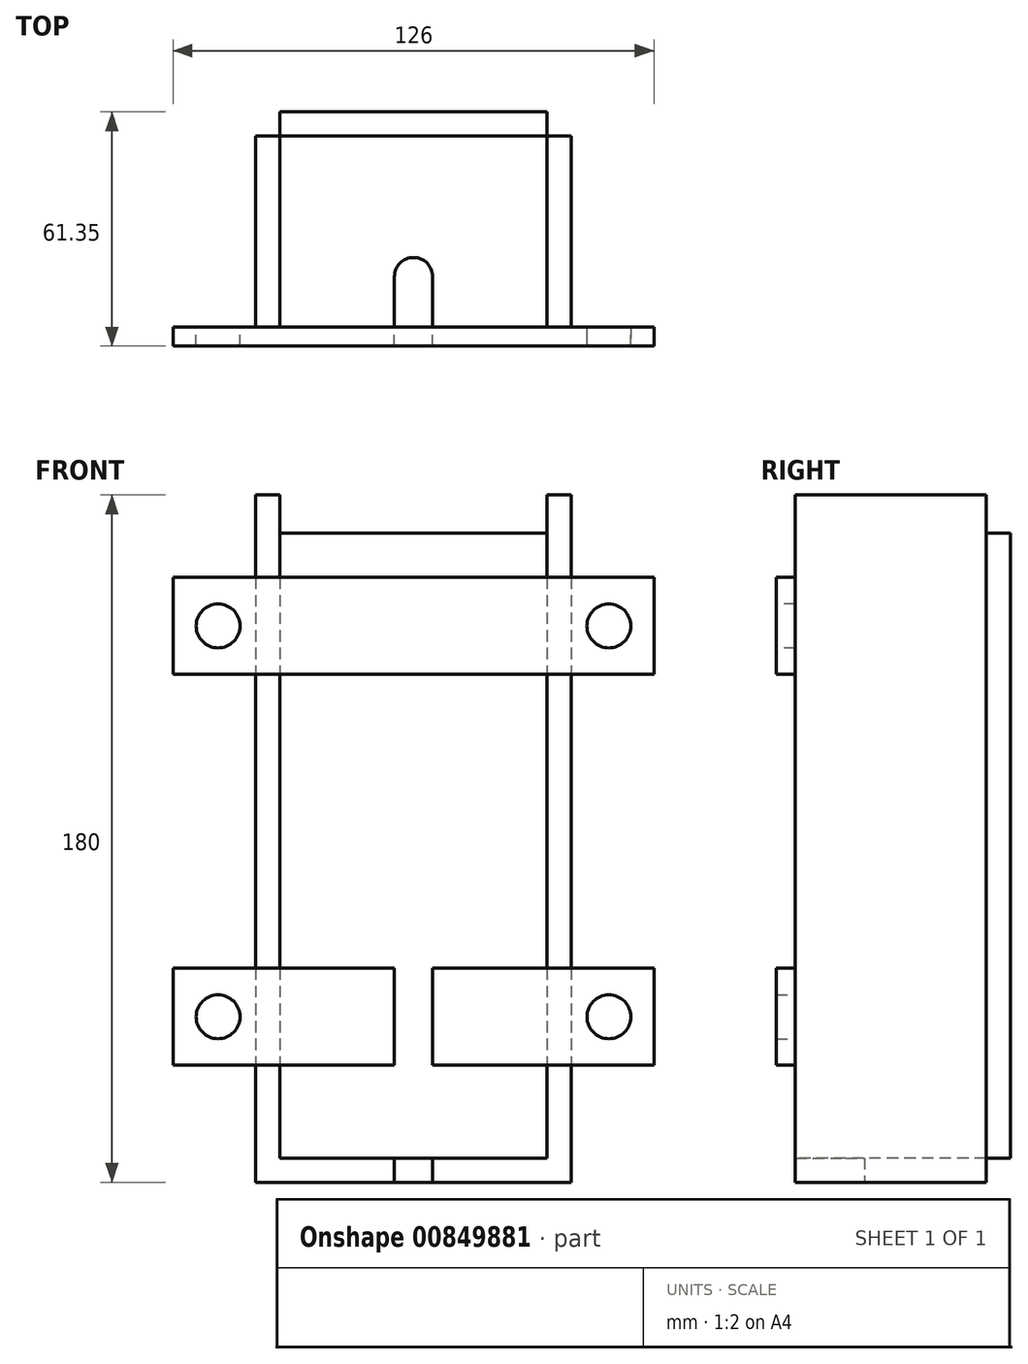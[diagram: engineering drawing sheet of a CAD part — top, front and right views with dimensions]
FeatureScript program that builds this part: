
annotation { "Feature Type Name" : "Feature", "Feature Type Description" : "" }
export const myFeature = defineFeature(function(context is Context, id is Id, definition is map)
    precondition{}
    {
        {
            var Q0;
            Q0=qCreatedBy(makeId("Top.planeOp"),FACE);
            var sketch = newSketch(context, id + "F0", { "sketchPlane" : qUnion([Q0])});
            skPoint(sketch, "E0.middle", {"position": v(0, 0) * mm});
            skLineSegment(sketch, "E1.bottom", {"start": v(35, 25) * mm, "end": v(-35, 25) * mm});
            skLineSegment(sketch, "E1.top", {"start": v(35, -25) * mm, "end": v(-35, -25) * mm});
            skLineSegment(sketch, "E1.left", {"start": v(35, 25) * mm, "end": v(35, -25) * mm});
            skLineSegment(sketch, "E1.right", {"start": v(-35, 25) * mm, "end": v(-35, -25) * mm});
            skLineSegment(sketch, "E2", {"start": v(0, -25) * mm, "end": v(-35, -25) * mm});
            skLineSegment(sketch, "E3", {"start": v(-35, -25) * mm, "end": v(-5, -25) * mm});
            skLineSegment(sketch, "E4", {"start": v(35, -25) * mm, "end": v(5, -25) * mm});
            skLineSegment(sketch, "E5", {"start": v(-5, -25) * mm, "end": v(-5, -11.8) * mm});
            skLineSegment(sketch, "E6", {"start": v(5, -25) * mm, "end": v(5, -11.8) * mm});
            skArc(sketch, "E7", {"start": v(-5, -11.8) * mm, "mid": v(0, -6.8) * mm, "end": v(5, -11.8) * mm});
            skSolve(sketch);
        }
        {
            var Q0;
            Q0=makeQuery(id+"F0.imprint","IMPRINT",FACE,{"disambiguationData":[TD([[makeQuery(id+"F0.imprint","IMPRINT",EDGE,{"derivedFrom":sQuery(id+"F0.wireOp",EDGE,"E1.bottom")}),1.0]])]});
            extrude(context, id + "F1", {"entities" : qUnion([Q0]), "depth" : 6.35 * mm, "offsetDistance" : 25 * mm});
        }
        {
            var Q0;
            Q0=makeQuery(id+"F1.opExtrude","SWEPT_FACE",FACE,{"disambiguationData":[OSD([sQuery(id+"F0.wireOp",EDGE,"E1.right")])]});
            var sketch = newSketch(context, id + "F2", { "sketchPlane" : qUnion([Q0])});
            skLineSegment(sketch, "E8.bottom", {"start": v(-25, 0) * mm, "end": v(25, 0) * mm});
            skLineSegment(sketch, "E8.top", {"start": v(-25, 180) * mm, "end": v(25, 180) * mm});
            skLineSegment(sketch, "E8.left", {"start": v(-25, 0) * mm, "end": v(-25, 180) * mm});
            skLineSegment(sketch, "E8.right", {"start": v(25, 0) * mm, "end": v(25, 180) * mm});
            skSolve(sketch);
        }
        {
            var Q0;
            Q0=qSketchRegion(id+"F2",true);
            extrude(context, id + "F3", {"entities" : qUnion([Q0]), "operationType" : NewBodyOperationType.ADD, "depth" : 6.35 * mm, "offsetDistance" : 25 * mm});
        }
        {
            var Q0;
            Q0=makeQuery(id+"F1.opExtrude","SWEPT_FACE",FACE,{"disambiguationData":[OSD([sQuery(id+"F0.wireOp",EDGE,"E1.left")])]});
            var sketch = newSketch(context, id + "F4", { "sketchPlane" : qUnion([Q0])});
            skLineSegment(sketch, "E9.bottom", {"start": v(-25, 0) * mm, "end": v(25, 0) * mm});
            skLineSegment(sketch, "E9.top", {"start": v(-25, 180) * mm, "end": v(25, 180) * mm});
            skLineSegment(sketch, "E9.left", {"start": v(-25, 0) * mm, "end": v(-25, 180) * mm});
            skLineSegment(sketch, "E9.right", {"start": v(25, 0) * mm, "end": v(25, 180) * mm});
            skSolve(sketch);
        }
        {
            var Q0;
            Q0=qSketchRegion(id+"F4",true);
            extrude(context, id + "F5", {"entities" : qUnion([Q0]), "operationType" : NewBodyOperationType.ADD, "depth" : 6.35 * mm, "offsetDistance" : 25 * mm});
        }
        {
            var Q0;
            Q0=makeQuery(id+"F5.boolean.opBoolean","MERGE",FACE,{"derivedFrom":[makeQuery(id+"F3.boolean.opBoolean","MERGE",FACE,{"derivedFrom":[makeQuery(id+"F1.opExtrude","SWEPT_FACE",FACE,{"disambiguationData":[OSD([sQuery(id+"F0.wireOp",EDGE,"E1.bottom")])]}),makeQuery(id+"F3.opExtrude","SWEPT_FACE",FACE,{"disambiguationData":[OSD([sQuery(id+"F2.wireOp",EDGE,"E8.left")])]})]}),makeQuery(id+"F5.opExtrude","SWEPT_FACE",FACE,{"disambiguationData":[OSD([sQuery(id+"F4.wireOp",EDGE,"E9.right")])]})]});
            var sketch = newSketch(context, id + "F6", { "sketchPlane" : qUnion([Q0])});
            skLineSegment(sketch, "E10.bottom", {"start": v(41.35, 0) * mm, "end": v(-41.35, 0) * mm});
            skLineSegment(sketch, "E10.top", {"start": v(41.35, 180) * mm, "end": v(-41.35, 180) * mm});
            skLineSegment(sketch, "E10.left", {"start": v(41.35, 0) * mm, "end": v(41.35, 180) * mm});
            skLineSegment(sketch, "E10.right", {"start": v(-41.35, 0) * mm, "end": v(-41.35, 180) * mm});
            skLineSegment(sketch, "E11.bottom", {"start": v(-41.35, 0) * mm, "end": v(41.35, 0) * mm});
            skLineSegment(sketch, "E11.top", {"start": v(-41.35, 170) * mm, "end": v(41.35, 170) * mm});
            skLineSegment(sketch, "E11.left", {"start": v(-41.35, 0) * mm, "end": v(-41.35, 170) * mm});
            skLineSegment(sketch, "E11.right", {"start": v(41.35, 0) * mm, "end": v(41.35, 170) * mm});
            skSolve(sketch);
        }
        {
            var Q0;
            {var subQ5=makeQuery(id+"F1.opExtrude","CAP_EDGE",EDGE,{"disambiguationData":[OSD([sQuery(id+"F0.wireOp",EDGE,"E1.bottom")])],"isStart":false});Q0=makeQuery(id+"F6.imprint","IMPRINT",FACE,{"disambiguationData":[TD([[makeQuery(id+"F6.imprint","IMPRINT",EDGE,{"derivedFrom":subQ5}),1.0]])]});}
            var Q1;
            Q1=makeQuery(id+"F6.imprint","IMPRINT",FACE,{"disambiguationData":[TD([[makeQuery(id+"F6.imprint","IMPRINT",EDGE,{"derivedFrom":sQuery(id+"F6.wireOp",EDGE,"E11.bottom")}),1.0]])]});
            var Q2;
            Q2=qSketchRegion(id+"F8",true);
            extrude(context, id + "F7", {"entities" : qUnion([Q0, Q1, Q2]), "operationType" : NewBodyOperationType.ADD, "depth" : 6.35 * mm, "offsetDistance" : 25 * mm});
        }
        {
            var Q0;
            Q0=makeQuery(id+"F5.boolean.opBoolean","MERGE",FACE,{"derivedFrom":[makeQuery(id+"F1.opExtrude","SWEPT_FACE",FACE,{"disambiguationData":[OSD([sQuery(id+"F0.wireOp",EDGE,"E4")])]}),makeQuery(id+"F5.opExtrude","SWEPT_FACE",FACE,{"disambiguationData":[OSD([sQuery(id+"F4.wireOp",EDGE,"E9.left")])]})]});
            var sketch = newSketch(context, id + "F8", { "sketchPlane" : qUnion([Q0])});
            skLineSegment(sketch, "E12", {"start": v(5, 6.35) * mm, "end": v(5, 43.33) * mm});
            skLineSegment(sketch, "E13", {"start": v(5, 43.33) * mm, "end": v(51.2, 43.33) * mm});
            skLineSegment(sketch, "E14", {"start": v(5, 6.35) * mm, "end": v(5, 30.62) * mm});
            skLineSegment(sketch, "E15.bottom", {"start": v(5, 30.62) * mm, "end": v(63, 30.62) * mm});
            skLineSegment(sketch, "E15.top", {"start": v(5, 56.03) * mm, "end": v(63, 56.03) * mm});
            skLineSegment(sketch, "E15.left", {"start": v(5, 30.62) * mm, "end": v(5, 56.03) * mm});
            skLineSegment(sketch, "E15.right", {"start": v(63, 30.63) * mm, "end": v(63, 56.02) * mm});
            skCircle(sketch, "E16", {"center": v(51.2, 43.33) * mm, "radius": 5.75 * mm});
            skLineSegment(sketch, "E17", {"start": v(5, 30.62) * mm, "end": v(-5, 30.62) * mm});
            skLineSegment(sketch, "E18.bottom", {"start": v(-5, 30.62) * mm, "end": v(-63, 30.62) * mm});
            skLineSegment(sketch, "E18.top", {"start": v(-5, 56.03) * mm, "end": v(-63, 56.03) * mm});
            skLineSegment(sketch, "E18.left", {"start": v(-5, 30.62) * mm, "end": v(-5, 56.03) * mm});
            skLineSegment(sketch, "E18.right", {"start": v(-63, 30.62) * mm, "end": v(-63, 56.03) * mm});
            skLineSegment(sketch, "E19", {"start": v(-5, 43.33) * mm, "end": v(-51.19, 43.33) * mm});
            skCircle(sketch, "E20", {"center": v(-51.19, 43.33) * mm, "radius": 5.75 * mm});
            skLineSegment(sketch, "E21.bottom", {"start": v(-5, 30.62) * mm, "end": v(5, 30.62) * mm});
            skLineSegment(sketch, "E21.top", {"start": v(-5, 56.03) * mm, "end": v(5, 56.03) * mm});
            skSolve(sketch);
        }
        {
            var Q0;
            {var subQ1=sQuery(id+"F8.wireOp",EDGE,"E18.bottom");Q0=makeQuery(id+"F8.imprint","IMPRINT",FACE,{"disambiguationData":[TD([[makeQuery(id+"F8.imprint","IMPRINT",EDGE,{"derivedFrom":subQ1}),-1.0]])]});}
            var Q1;
            {var subQ3=sQuery(id+"F8.wireOp",EDGE,"E21.bottom");Q1=makeQuery(id+"F8.imprint","IMPRINT",FACE,{"disambiguationData":[TD([[makeQuery(id+"F8.imprint","IMPRINT",EDGE,{"derivedFrom":subQ3}),1.0]])]});}
            var Q2;
            {var subQ0=sQuery(id+"F8.wireOp",EDGE,"E15.right");Q2=makeQuery(id+"F8.imprint","IMPRINT",FACE,{"disambiguationData":[TD([[makeQuery(id+"F8.imprint","IMPRINT",EDGE,{"derivedFrom":subQ0}),1.0]])]});}
            var Q3;
            {var subQ0=sQuery(id+"F8.wireOp",EDGE,"E13");var subQ1=sQuery(id+"F4.wireOp",EDGE,"E9.left");var subQ2=makeQuery(id+"F5.opExtrude","CAP_EDGE",EDGE,{"disambiguationData":[OSD([subQ1])],"isStart":false});var subQ3=makeQuery(id+"F8.imprint","INTERSECT",VERTEX,{"derivedFrom":[subQ2,subQ0]});Q3=makeQuery(id+"F8.imprint","IMPRINT",FACE,{"disambiguationData":[TD([[makeQuery(id+"F8.imprint","IMPRINT",EDGE,{"disambiguationData":[TD([[subQ3,1.0]])],"derivedFrom":subQ0}),1.0]])]});}
            var Q4;
            {var subQ0=sQuery(id+"F8.wireOp",EDGE,"E13");var subQ1=sQuery(id+"F4.wireOp",EDGE,"E9.left");var subQ2=makeQuery(id+"F5.opExtrude","CAP_EDGE",EDGE,{"disambiguationData":[OSD([subQ1])],"isStart":false});var subQ3=makeQuery(id+"F8.imprint","INTERSECT",VERTEX,{"derivedFrom":[subQ2,subQ0]});Q4=makeQuery(id+"F8.imprint","IMPRINT",FACE,{"disambiguationData":[TD([[makeQuery(id+"F8.imprint","IMPRINT",EDGE,{"disambiguationData":[TD([[subQ3,1.0]])],"derivedFrom":subQ0}),-1.0]])]});}
            var Q5;
            {var subQ0=sQuery(id+"F8.wireOp",EDGE,"E15.left");var subQ1=sQuery(id+"F8.wireOp",EDGE,"E13");var subQ2=makeQuery(id+"F8.imprint","INTERSECT",VERTEX,{"derivedFrom":[subQ1,subQ0]});Q5=makeQuery(id+"F8.imprint","IMPRINT",FACE,{"disambiguationData":[TD([[makeQuery(id+"F8.imprint","IMPRINT",EDGE,{"disambiguationData":[TD([[subQ2,-1.0]])],"derivedFrom":subQ1}),-1.0]])]});}
            var Q6;
            {var subQ0=sQuery(id+"F8.wireOp",EDGE,"E15.left");var subQ1=sQuery(id+"F8.wireOp",EDGE,"E13");var subQ2=makeQuery(id+"F8.imprint","INTERSECT",VERTEX,{"derivedFrom":[subQ1,subQ0]});Q6=makeQuery(id+"F8.imprint","IMPRINT",FACE,{"disambiguationData":[TD([[makeQuery(id+"F8.imprint","IMPRINT",EDGE,{"disambiguationData":[TD([[subQ2,-1.0]])],"derivedFrom":subQ1}),1.0]])]});}
            extrude(context, id + "F9", {"entities" : qUnion([Q0, Q1, Q2, Q3, Q4, Q5, Q6]), "operationType" : NewBodyOperationType.ADD, "depth" : 5 * mm, "offsetDistance" : 25 * mm});
        }
        {
            var Q0;
            Q0=makeQuery(id+"F9.opExtrude","CAP_FACE",FACE,{"disambiguationData":[OSD([sQuery(id+"F8.wireOp",EDGE,"E15.bottom"),sQuery(id+"F8.wireOp",EDGE,"E15.top"),sQuery(id+"F8.wireOp",EDGE,"E15.right"),sQuery(id+"F8.wireOp",EDGE,"E16"),sQuery(id+"F8.wireOp",EDGE,"E18.bottom"),sQuery(id+"F8.wireOp",EDGE,"E18.top"),sQuery(id+"F8.wireOp",EDGE,"E18.right"),sQuery(id+"F8.wireOp",EDGE,"E20"),sQuery(id+"F8.wireOp",EDGE,"E21.bottom"),sQuery(id+"F8.wireOp",EDGE,"E21.top")])],"isStart":false});
            var sketch = newSketch(context, id + "F10", { "sketchPlane" : qUnion([Q0])});
            skLineSegment(sketch, "E22", {"start": v(-51.2, 43.33) * mm, "end": v(-51.2, 145.7) * mm});
            skCircle(sketch, "E23", {"center": v(-51.2, 145.7) * mm, "radius": 5.75 * mm});
            skLineSegment(sketch, "E24", {"start": v(-63, 56.03) * mm, "end": v(-63, 133) * mm});
            skLineSegment(sketch, "E25.bottom", {"start": v(-63, 133) * mm, "end": v(63, 133) * mm});
            skLineSegment(sketch, "E25.top", {"start": v(-63, 158.4) * mm, "end": v(63, 158.4) * mm});
            skLineSegment(sketch, "E25.left", {"start": v(-63, 133) * mm, "end": v(-63, 158.4) * mm});
            skLineSegment(sketch, "E25.right", {"start": v(63, 133) * mm, "end": v(63, 158.4) * mm});
            skLineSegment(sketch, "E26", {"start": v(-51.2, 145.7) * mm, "end": v(51.18, 145.7) * mm});
            skCircle(sketch, "E27", {"center": v(51.18, 145.7) * mm, "radius": 5.75 * mm});
            skSolve(sketch);
        }
        {
            var Q0;
            Q0=makeQuery(id+"F10.imprint","IMPRINT",FACE,{"disambiguationData":[TD([[makeQuery(id+"F10.imprint","IMPRINT",EDGE,{"derivedFrom":sQuery(id+"F10.wireOp",EDGE,"2UdgNEkt-0Pvw-VFGa-zIAp-KuCJepWeR8V2")}),-1.0]])]});
            var Q1;
            Q1=makeQuery(id+"F10.imprint","IMPRINT",FACE,{"disambiguationData":[TD([[makeQuery(id+"F10.imprint","IMPRINT",EDGE,{"derivedFrom":sQuery(id+"F10.wireOp",EDGE,"E25.top")}),-1.0]])]});
            extrude(context, id + "F11", {"entities" : qUnion([Q0, Q1]), "operationType" : NewBodyOperationType.ADD, "oppositeDirection" : true, "depth" : 5 * mm, "offsetDistance" : 25 * mm});
        }
    });
